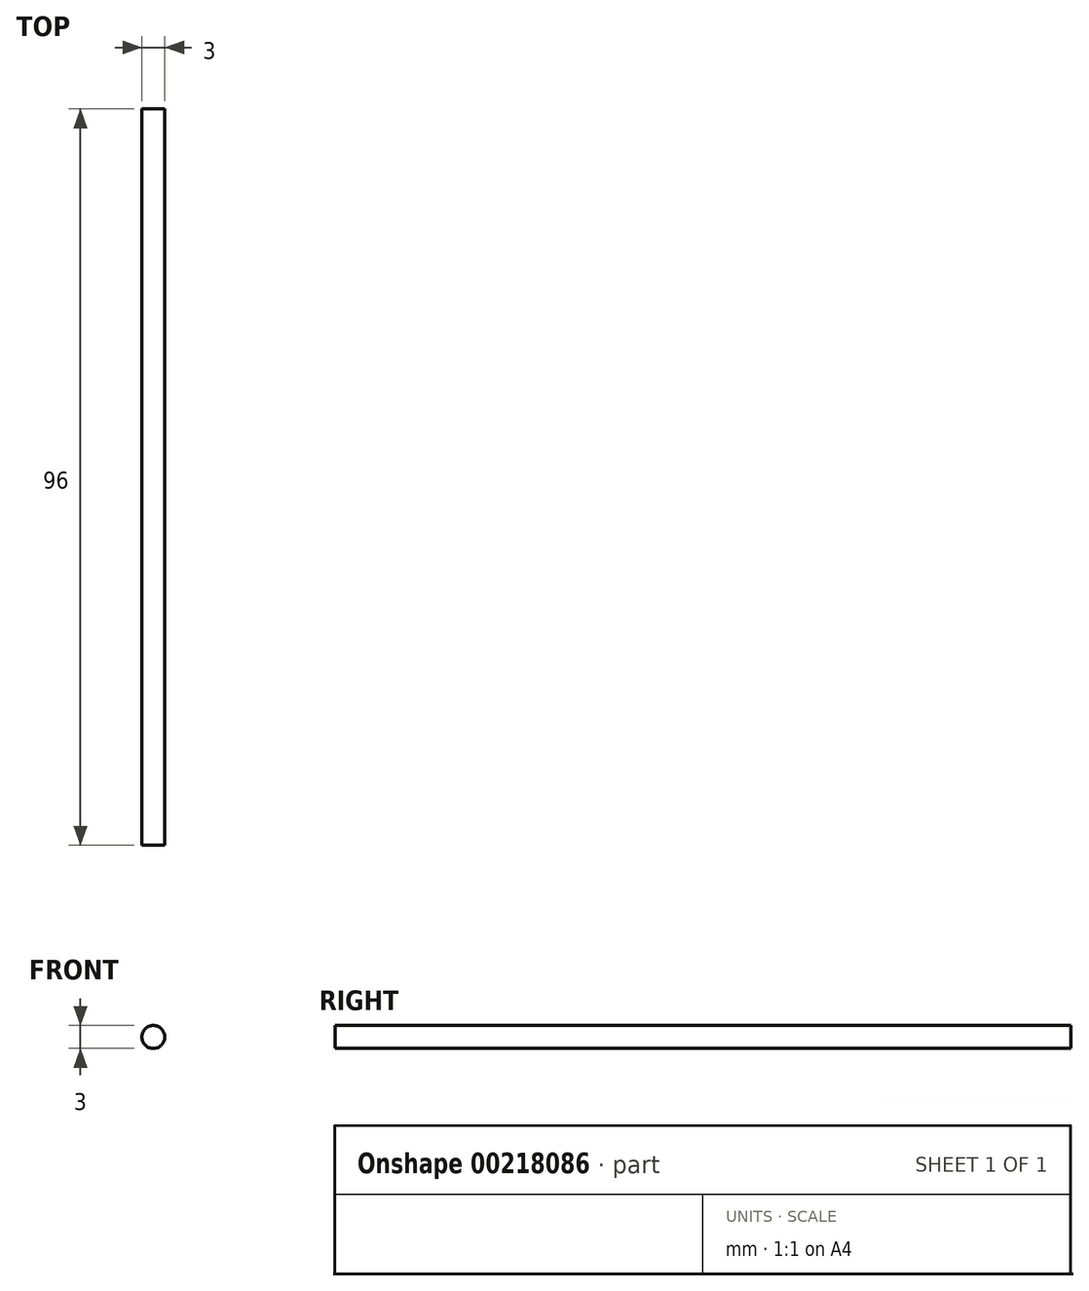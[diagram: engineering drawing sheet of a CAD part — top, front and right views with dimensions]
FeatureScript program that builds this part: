
annotation { "Feature Type Name" : "Feature", "Feature Type Description" : "" }
export const myFeature = defineFeature(function(context is Context, id is Id, definition is map)
    precondition{}
    {
        {
            var Q0;
            Q0=qCreatedBy(makeId("Front.planeOp"),FACE);
            var sketch = newSketch(context, id + "F0", { "sketchPlane" : qUnion([Q0])});
            skCircle(sketch, "E0", {"center": v(18.68, 12.5) * mm, "radius": 1.5 * mm});
            skSolve(sketch);
        }
        {
            var Q0;
            Q0=makeQuery(id+"F0.imprint","IMPRINT",FACE,{"disambiguationData":[TD([[makeQuery(id+"F0.imprint","IMPRINT",EDGE,{"derivedFrom":sQuery(id+"F0.wireOp",EDGE,"E0")}),1.0]])]});
            extrude(context, id + "F1", {"entities" : qUnion([Q0]), "depth" : 96 * mm});
        }
    });
